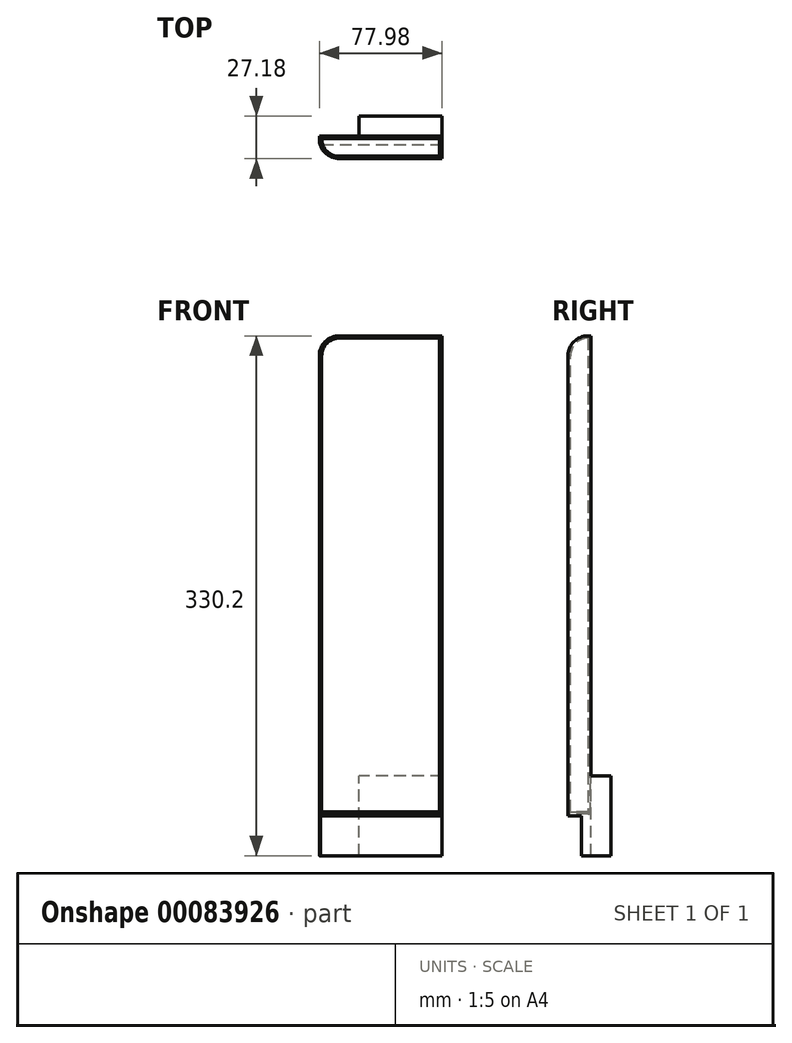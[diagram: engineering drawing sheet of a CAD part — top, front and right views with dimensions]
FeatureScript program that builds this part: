
annotation { "Feature Type Name" : "Feature", "Feature Type Description" : "" }
export const myFeature = defineFeature(function(context is Context, id is Id, definition is map)
    precondition{}
    {
        {
            var Q0;
            Q0=qCreatedBy(makeId("Front.planeOp"),FACE);
            var sketch = newSketch(context, id + "F0", { "sketchPlane" : qUnion([Q0])});
            skLineSegment(sketch, "E0.bottom", {"start": v(76.2, 304.8) * mm, "end": v(0, 304.8) * mm});
            skLineSegment(sketch, "E0.top", {"start": v(76.2, 0) * mm, "end": v(0, 0) * mm});
            skLineSegment(sketch, "E0.left", {"start": v(76.2, 304.8) * mm, "end": v(76.2, 0) * mm});
            skLineSegment(sketch, "E0.right", {"start": v(0, 304.8) * mm, "end": v(0, 0) * mm});
            skSolve(sketch);
        }
        {
            var Q0;
            Q0 = qSketchRegion(id + "F0", true);
            extrude(context, id + "F1", {"entities" : qUnion([Q0]), "depth" : 1.78 * mm});
        }
        {
            var Q0;
            Q0=makeQuery(id+"F1.opExtrude","CAP_FACE",FACE,{"disambiguationData":[OSD([sQuery(id+"F0.wireOp",EDGE,"E0.bottom"),sQuery(id+"F0.wireOp",EDGE,"E0.top"),sQuery(id+"F0.wireOp",EDGE,"E0.left"),sQuery(id+"F0.wireOp",EDGE,"E0.right")])],"isStart":false});
            var sketch = newSketch(context, id + "F2", { "sketchPlane" : qUnion([Q0])});
            skLineSegment(sketch, "E1.bottom", {"start": v(0, 0) * mm, "end": v(76.2, 0) * mm});
            skLineSegment(sketch, "E1.top", {"start": v(0, 2.54) * mm, "end": v(76.2, 2.54) * mm});
            skLineSegment(sketch, "E1.left", {"start": v(0, 0) * mm, "end": v(0, 2.54) * mm});
            skLineSegment(sketch, "E1.right", {"start": v(76.2, 0) * mm, "end": v(76.2, 2.54) * mm});
            skSolve(sketch);
        }
        {
            var Q0;
            Q0 = qSketchRegion(id + "F2", true);
            extrude(context, id + "F3", {"entities" : qUnion([Q0]), "operationType" : NewBodyOperationType.ADD, "depth" : 12.7 * mm});
        }
        {
            var Q0;
            Q0=makeQuery(id+"F3.boolean.opBoolean","MERGE",FACE,{"derivedFrom":[makeQuery(id+"F1.opExtrude","SWEPT_FACE",FACE,{"disambiguationData":[OSD([sQuery(id+"F0.wireOp",EDGE,"E0.left")])]}),makeQuery(id+"F3.opExtrude","SWEPT_FACE",FACE,{"disambiguationData":[OSD([sQuery(id+"F2.wireOp",EDGE,"E1.right")])]})]});
            var sketch = newSketch(context, id + "F4", { "sketchPlane" : qUnion([Q0])});
            skLineSegment(sketch, "E2.bottom", {"start": v(0, 0) * mm, "end": v(-14.48, 0) * mm});
            skLineSegment(sketch, "E2.top", {"start": v(0, 304.8) * mm, "end": v(-14.48, 304.8) * mm});
            skLineSegment(sketch, "E2.left", {"start": v(0, 0) * mm, "end": v(0, 304.8) * mm});
            skLineSegment(sketch, "E2.right", {"start": v(-14.48, 0) * mm, "end": v(-14.48, 304.8) * mm});
            skLineSegment(sketch, "E3.bottom", {"start": v(1.1, 0.62) * mm, "end": v(1.22, 0.62) * mm});
            skLineSegment(sketch, "E3.top", {"start": v(1.1, 0.53) * mm, "end": v(1.22, 0.53) * mm});
            skLineSegment(sketch, "E3.left", {"start": v(1.1, 0.62) * mm, "end": v(1.1, 0.53) * mm});
            skLineSegment(sketch, "E3.right", {"start": v(1.22, 0.62) * mm, "end": v(1.22, 0.53) * mm});
            skSolve(sketch);
        }
        {
            var Q0;
            Q0 = qSketchRegion(id + "F4", true);
            extrude(context, id + "F5", {"entities" : qUnion([Q0]), "operationType" : NewBodyOperationType.ADD, "depth" : 1.78 * mm});
        }
        {
            var Q0;
            Q0=makeQuery(id+"F5.boolean.opBoolean","MERGE",FACE,{"derivedFrom":[makeQuery(id+"F3.boolean.opBoolean","MERGE",FACE,{"derivedFrom":[makeQuery(id+"F1.opExtrude","SWEPT_FACE",FACE,{"disambiguationData":[OSD([sQuery(id+"F0.wireOp",EDGE,"E0.top")])]}),makeQuery(id+"F3.opExtrude","SWEPT_FACE",FACE,{"disambiguationData":[OSD([sQuery(id+"F2.wireOp",EDGE,"E1.bottom")])]})]}),makeQuery(id+"F5.opExtrude","SWEPT_FACE",FACE,{"disambiguationData":[OSD([sQuery(id+"F4.wireOp",EDGE,"E2.bottom")])]})]});
            var sketch = newSketch(context, id + "F6", { "sketchPlane" : qUnion([Q0])});
            skLineSegment(sketch, "E4.bottom", {"start": v(77.98, 0) * mm, "end": v(0, 0) * mm});
            skLineSegment(sketch, "E4.top", {"start": v(77.98, 5.84) * mm, "end": v(0, 5.84) * mm});
            skLineSegment(sketch, "E4.left", {"start": v(77.98, 0) * mm, "end": v(77.98, 5.84) * mm});
            skLineSegment(sketch, "E4.right", {"start": v(0, 0) * mm, "end": v(0, 5.84) * mm});
            skSolve(sketch);
        }
        {
            var Q0;
            Q0 = qSketchRegion(id + "F6", true);
            extrude(context, id + "F7", {"entities" : qUnion([Q0]), "operationType" : NewBodyOperationType.ADD, "depth" : 25.4 * mm});
        }
        {
            var Q0;
            Q0=makeQuery(id+"F7.boolean.opBoolean","MERGE",FACE,{"derivedFrom":[makeQuery(id+"F5.boolean.opBoolean","MERGE",FACE,{"derivedFrom":[makeQuery(id+"F1.opExtrude","CAP_FACE",FACE,{"disambiguationData":[OSD([sQuery(id+"F0.wireOp",EDGE,"E0.bottom"),sQuery(id+"F0.wireOp",EDGE,"E0.top"),sQuery(id+"F0.wireOp",EDGE,"E0.left"),sQuery(id+"F0.wireOp",EDGE,"E0.right")])],"isStart":true}),makeQuery(id+"F5.opExtrude","SWEPT_FACE",FACE,{"disambiguationData":[OSD([sQuery(id+"F4.wireOp",EDGE,"E2.left")])]})]}),makeQuery(id+"F7.opExtrude","SWEPT_FACE",FACE,{"disambiguationData":[OSD([sQuery(id+"F6.wireOp",EDGE,"E4.bottom")])]})]});
            var sketch = newSketch(context, id + "F8", { "sketchPlane" : qUnion([Q0])});
            skLineSegment(sketch, "E5.bottom", {"start": v(-77.98, -25.4) * mm, "end": v(-25.65, -25.4) * mm});
            skLineSegment(sketch, "E5.top", {"start": v(-77.98, 25.4) * mm, "end": v(-25.65, 25.4) * mm});
            skLineSegment(sketch, "E5.left", {"start": v(-77.98, -25.4) * mm, "end": v(-77.98, 25.4) * mm});
            skLineSegment(sketch, "E5.right", {"start": v(-25.65, -25.4) * mm, "end": v(-25.65, 25.4) * mm});
            skSolve(sketch);
        }
        {
            var Q0;
            Q0 = qSketchRegion(id + "F8", true);
            extrude(context, id + "F9", {"entities" : qUnion([Q0]), "depth" : 10.16 * mm});
        }
        {
            var Q0;
            Q0=makeQuery(id+"F9.opExtrude","SWEPT_BODY",BODY,{"disambiguationData":[OSD([sQuery(id+"F8.wireOp",EDGE,"E5.bottom"),sQuery(id+"F8.wireOp",EDGE,"E5.top"),sQuery(id+"F8.wireOp",EDGE,"E5.left"),sQuery(id+"F8.wireOp",EDGE,"E5.right")])]});
            var Q1;
            Q1=makeQuery(id+"F5.opExtrude","SWEPT_BODY",BODY,{"disambiguationData":[OSD([sQuery(id+"F4.wireOp",EDGE,"E3.bottom"),sQuery(id+"F4.wireOp",EDGE,"E3.top"),sQuery(id+"F4.wireOp",EDGE,"E3.left"),sQuery(id+"F4.wireOp",EDGE,"E3.right")])]});
            deleteBodies(context, id + "F10", {"entities" : qUnion([Q0, Q1])});
        }
        {
            var Q0;
            Q0=makeQuery(id+"F7.boolean.opBoolean","MERGE",FACE,{"derivedFrom":[makeQuery(id+"F5.boolean.opBoolean","MERGE",FACE,{"derivedFrom":[makeQuery(id+"F1.opExtrude","CAP_FACE",FACE,{"disambiguationData":[OSD([sQuery(id+"F0.wireOp",EDGE,"E0.bottom"),sQuery(id+"F0.wireOp",EDGE,"E0.top"),sQuery(id+"F0.wireOp",EDGE,"E0.left"),sQuery(id+"F0.wireOp",EDGE,"E0.right")])],"isStart":true}),makeQuery(id+"F5.opExtrude","SWEPT_FACE",FACE,{"disambiguationData":[OSD([sQuery(id+"F4.wireOp",EDGE,"E2.left")])]})]}),makeQuery(id+"F7.opExtrude","SWEPT_FACE",FACE,{"disambiguationData":[OSD([sQuery(id+"F6.wireOp",EDGE,"E4.bottom")])]})]});
            var sketch = newSketch(context, id + "F11", { "sketchPlane" : qUnion([Q0])});
            skLineSegment(sketch, "E6.bottom", {"start": v(-77.98, -25.4) * mm, "end": v(-25.15, -25.4) * mm});
            skLineSegment(sketch, "E6.top", {"start": v(-77.98, 25.4) * mm, "end": v(-25.15, 25.4) * mm});
            skLineSegment(sketch, "E6.left", {"start": v(-77.98, -25.4) * mm, "end": v(-77.98, 25.4) * mm});
            skLineSegment(sketch, "E6.right", {"start": v(-25.15, -25.4) * mm, "end": v(-25.15, 25.4) * mm});
            skSolve(sketch);
        }
        {
            var Q0;
            Q0 = qSketchRegion(id + "F11", true);
            extrude(context, id + "F12", {"entities" : qUnion([Q0]), "operationType" : NewBodyOperationType.ADD, "depth" : 12.7 * mm});
        }
        {
            var Q0;
            Q0=makeQuery(id+"F1.opExtrude","SWEPT_EDGE",EDGE,{"disambiguationData":[OSD([sQuery(id+"F0.wireOp",EDGE,"E0.bottom"),sQuery(id+"F0.wireOp",EDGE,"E0.right")])]});
            fillet(context, id + "F13", {"entities" : qUnion([Q0]), "radius" : 12.7 * mm, "tangentPropagation" : true, "allowEdgeOverflow" : false});
        }
        {
            var Q0;
            Q0=makeQuery(id+"F5.opExtrude","SWEPT_EDGE",EDGE,{"disambiguationData":[OSD([sQuery(id+"F4.wireOp",EDGE,"E2.top"),sQuery(id+"F4.wireOp",EDGE,"E2.right")])]});
            fillet(context, id + "F14", {"entities" : qUnion([Q0]), "radius" : 12.7 * mm, "tangentPropagation" : true, "allowEdgeOverflow" : false});
        }
        {
            var Q0;
            Q0=makeQuery(id+"F3.opExtrude","CAP_EDGE",EDGE,{"disambiguationData":[OSD([sQuery(id+"F2.wireOp",EDGE,"E1.left")])],"isStart":false});
            fillet(context, id + "F15", {"entities" : qUnion([Q0]), "radius" : 12.7 * mm, "tangentPropagation" : true, "allowEdgeOverflow" : false});
        }
        {
            var Q0;
            Q0=makeQuery(id+"F1.opExtrude","CAP_EDGE",EDGE,{"disambiguationData":[OSD([sQuery(id+"F0.wireOp",EDGE,"E0.right")])],"isStart":false});
            chamfer(context, id + "F16", {"entities" : qUnion([Q0]), "width" : 1.52 * mm, "tangentPropagation" : true});
        }
        {
            var Q0;
            Q0=makeQuery(id+"F3.opExtrude","SWEPT_EDGE",EDGE,{"disambiguationData":[OSD([sQuery(id+"F0.wireOp",EDGE,"E0.right"),sQuery(id+"F2.wireOp",EDGE,"E1.top"),sQuery(id+"F2.wireOp",EDGE,"E1.left")])]});
            var Q1;
            Q1=makeQuery(id+"F3.opExtrude","CAP_EDGE",EDGE,{"disambiguationData":[OSD([sQuery(id+"F2.wireOp",EDGE,"E1.top")])],"isStart":false});
            var Q2;
            Q2=makeQuery(id+"F5.opExtrude","CAP_EDGE",EDGE,{"disambiguationData":[OSD([sQuery(id+"F4.wireOp",EDGE,"E2.right")])],"isStart":true});
            chamfer(context, id + "F17", {"entities" : qUnion([Q0, Q1, Q2]), "width" : 1.52 * mm, "tangentPropagation" : true});
        }
    });
